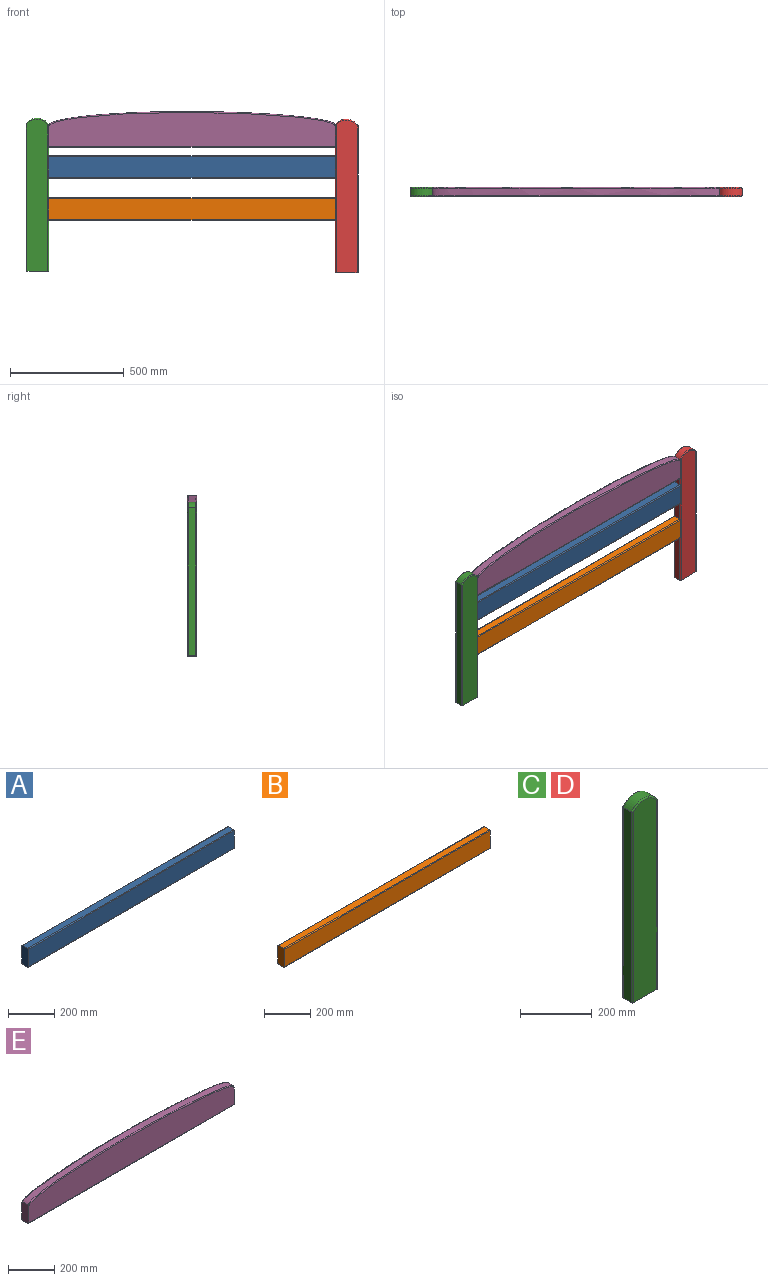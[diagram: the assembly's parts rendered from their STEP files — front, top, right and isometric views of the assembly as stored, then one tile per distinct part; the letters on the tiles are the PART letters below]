
ASSEMBLY  parts=5 mates=4
PART A: 10 faces, bbox 1260x40x100 mm
  f0: plane 1260x32mm, normal (0,0,1), area 40320mm2, adj f1,f3,f7,f9
  f1: plane 100x40mm, normal (-1,0,0), area 3986.3mm2, adj f0,f2,f4,f5,f6,f7,f8,f9
  f2: plane 1260x32mm, normal (0,0,-1), area 40320mm2, adj f1,f3,f6,f8
  f3: plane 100x40mm, normal (1,0,0), area 3986.3mm2, adj f0,f2,f4,f5,f6,f7,f8,f9
  f4: plane 1260x92mm, normal (0,-1,0), area 115920mm2, adj f1,f3,f8,f9
  f5: plane 1260x92mm, normal (0,1,0), area 115920mm2, adj f1,f3,f6,f7
  f6: cylinder r=4mm len=1260mm, axis (1,0,0), area 7916.8mm2, adj f1,f2,f3,f5
  f7: cylinder r=4mm len=1260mm, axis (-1,0,0), area 7916.8mm2, adj f0,f1,f3,f5
  f8: cylinder r=4mm len=1260mm, axis (-1,0,0), area 7916.8mm2, adj f1,f2,f3,f4
  f9: cylinder r=4mm len=1260mm, axis (1,0,0), area 7916.8mm2, adj f0,f1,f3,f4
PART B: 10 faces, bbox 1260x40x100 mm
  f0: plane 1260x32mm, normal (0,0,1), area 40320mm2, adj f1,f3,f7,f9
  f1: plane 100x40mm, normal (-1,0,0), area 3986.3mm2, adj f0,f2,f4,f5,f6,f7,f8,f9
  f2: plane 1260x32mm, normal (0,0,-1), area 40320mm2, adj f1,f3,f6,f8
  f3: plane 100x40mm, normal (1,0,0), area 3986.3mm2, adj f0,f2,f4,f5,f6,f7,f8,f9
  f4: plane 1260x92mm, normal (0,-1,0), area 115920mm2, adj f1,f3,f8,f9
  f5: plane 1260x92mm, normal (0,1,0), area 115920mm2, adj f1,f3,f6,f7
  f6: cylinder r=4mm len=1260mm, axis (1,0,0), area 7916.8mm2, adj f1,f2,f3,f5
  f7: cylinder r=4mm len=1260mm, axis (-1,0,0), area 7916.8mm2, adj f0,f1,f3,f5
  f8: cylinder r=4mm len=1260mm, axis (-1,0,0), area 7916.8mm2, adj f1,f2,f3,f4
  f9: cylinder r=4mm len=1260mm, axis (1,0,0), area 7916.8mm2, adj f0,f1,f3,f4
PART C: 12 faces, bbox 108.2x40x679.6 mm
  f0: plane 650x32mm, normal (-1,0,0), area 20800mm2, adj f1,f3,f6,f9
  f1: plane 100x40mm, normal (0,0,-1), area 3986.3mm2, adj f0,f2,f4,f5,f6,f8,f9,f11
  f2: plane 645.47x32mm, normal (1,0,0), area 20655.2mm2, adj f1,f3,f8,f11
  f3: cylinder r=60.05mm len=100mm, axis (0,1,0), area 3787.1mm2, adj f0,f2,f7,f10
  f4: plane 670.64x92mm, normal (0,-1,0), area 61036.5mm2, adj f1,f9,f10,f11
  f5: plane 670.64x92mm, normal (0,1,0), area 61036.5mm2, adj f1,f6,f7,f8
  f6: cylinder r=4mm len=650mm, axis (0,0,-1), area 4081.1mm2, adj f0,f1,f5,f7
  f7: torus R=56.05mm, axis (0,-1,0), area 720.1mm2, adj f3,f5,f6,f8
  f8: cylinder r=4mm len=645.47mm, axis (0,0,1), area 4053.1mm2, adj f1,f2,f5,f7
  f9: cylinder r=4mm len=650mm, axis (0,0,1), area 4081.1mm2, adj f0,f1,f4,f10
  f10: torus R=56.05mm, axis (0,-1,0), area 720.1mm2, adj f3,f4,f9,f11
  f11: cylinder r=4mm len=645.47mm, axis (0,0,-1), area 4053.1mm2, adj f1,f2,f4,f10
PART D: same geometry as C
PART E: 10 faces, bbox 1278x42.1x160.3 mm
  f0: plane 101.61x41.61mm, normal (-1,0,0), area 3982.7mm2, adj f1,f3,f4,f5,f6,f7,f8,f9
  f1: plane 1260x32mm, normal (0,0,-1), area 40320mm2, adj f0,f2,f6,f8
  f2: plane 102.09x42.09mm, normal (1,0,0), area 3979mm2, adj f1,f3,f4,f5,f6,f7,f8,f9
  f3: extruded ~1260x58.23mm, area 40755.5mm2, adj f0,f2,f7,f9
  f4: plane 1260.03x150.25mm, normal (0,-1,0), area 172407.4mm2, adj f0,f2,f8,f9
  f5: plane 1260.03x150.25mm, normal (0,1,0), area 172407.4mm2, adj f0,f2,f6,f7
  f6: cylinder r=4mm len=1260mm, axis (1,0,0), area 7916.8mm2, adj f0,f1,f2,f5
  f7: bspline ~1275.87x78.51mm, area 8022.4mm2, adj f0,f2,f3,f5
  f8: cylinder r=4mm len=1260mm, axis (-1,0,0), area 7916.8mm2, adj f0,f1,f2,f4
  f9: bspline ~1275.87x78.51mm, area 8022.4mm2, adj f0,f2,f3,f4
PLACE A t=(-97.86,0,6.33)mm
PLACE B t=(-97.86,0,3.43)mm
PLACE C at identity fixed
PLACE D t=(1360,0,-4.53)mm
PLACE E t=(-100.22,0,-19.85)mm
MATE fastened E.f2 <-> D.f0  axis (1,0,0) through (1248.62,-20,483.45)mm
MATE fastened C.f2 <-> A.f1  axis (1,0,0) through (-11.38,-20,-162.03)mm
MATE fastened E.f0 <-> C.f2  axis (-1,0,0) through (-11.38,-20,483.45)mm
MATE fastened B.f1 <-> C.f2  axis (-1,0,0) through (-11.38,-20,62.97)mm
